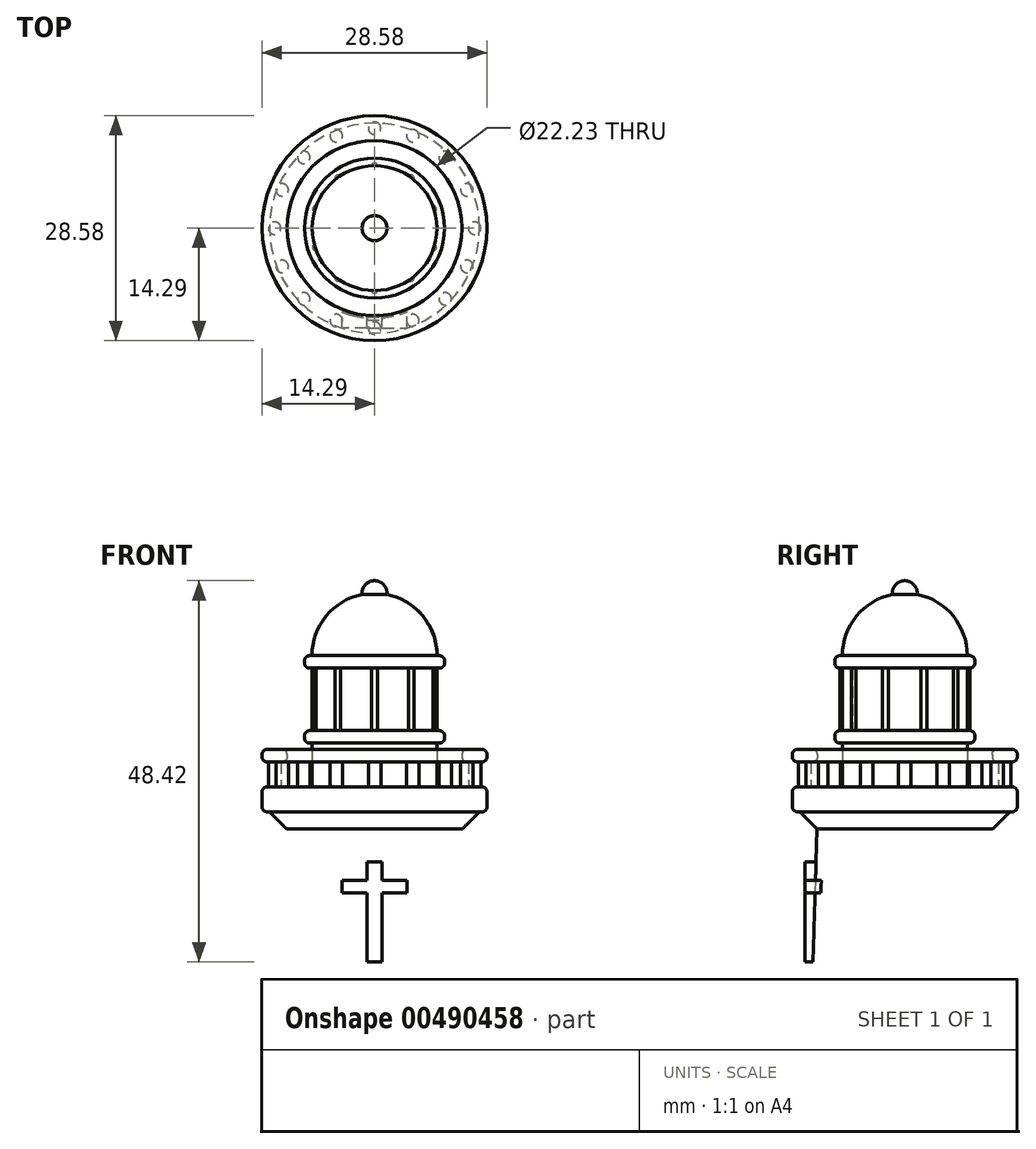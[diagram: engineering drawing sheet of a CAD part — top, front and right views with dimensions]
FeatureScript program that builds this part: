
annotation { "Feature Type Name" : "Feature", "Feature Type Description" : "" }
export const myFeature = defineFeature(function(context is Context, id is Id, definition is map)
    precondition{}
    {
        {
            var Q0;
            Q0=qCreatedBy(makeId("Top.planeOp"),FACE);
            var sketch = newSketch(context, id + "F0", { "sketchPlane" : qUnion([Q0])});
            skCircle(sketch, "E0.cCircle", {"center": v(0, 0) * mm, "radius": 25.4 * mm, "construction": true});
            skLineSegment(sketch, "E0.0", {"start": v(25.4, 14.66) * mm, "end": v(25.4, -14.66) * mm});
            skLineSegment(sketch, "E0.1", {"start": v(25.4, -14.66) * mm, "end": v(0, -29.33) * mm});
            skLineSegment(sketch, "E0.2", {"start": v(0, -29.33) * mm, "end": v(-25.4, -14.66) * mm});
            skLineSegment(sketch, "E0.3", {"start": v(-25.4, -14.66) * mm, "end": v(-25.4, 14.66) * mm});
            skLineSegment(sketch, "E0.4", {"start": v(-25.4, 14.66) * mm, "end": v(0, 29.33) * mm});
            skLineSegment(sketch, "E0.5", {"start": v(0, 29.33) * mm, "end": v(25.4, 14.66) * mm});
            skPoint(sketch, "E0.0.midPoint", {"position": v(25.4, 0) * mm});
            skSolve(sketch);
        }
        {
            var Q0;
            Q0 = qSketchRegion(id + "F0", true);
            extrude(context, id + "F1", {"entities" : qUnion([Q0]), "depth" : 3.17 * mm});
        }
        {
            var Q0;
            Q0=makeQuery(id+"F1.opExtrude","CAP_FACE",FACE,{"disambiguationData":[OSD([sQuery(id+"F0.wireOp",EDGE,"E0.0"),sQuery(id+"F0.wireOp",EDGE,"E0.1"),sQuery(id+"F0.wireOp",EDGE,"E0.2"),sQuery(id+"F0.wireOp",EDGE,"E0.3"),sQuery(id+"F0.wireOp",EDGE,"E0.4"),sQuery(id+"F0.wireOp",EDGE,"E0.5")])],"isStart":false});
            var sketch = newSketch(context, id + "F2", { "sketchPlane" : qUnion([Q0])});
            skCircle(sketch, "E1.cCircle", {"center": v(0, 0) * mm, "radius": 22.23 * mm, "construction": true});
            skLineSegment(sketch, "E1.0", {"start": v(22.23, 12.83) * mm, "end": v(22.23, -12.83) * mm});
            skLineSegment(sketch, "E1.1", {"start": v(22.23, -12.83) * mm, "end": v(0, -25.66) * mm});
            skLineSegment(sketch, "E1.2", {"start": v(0, -25.66) * mm, "end": v(-22.23, -12.83) * mm});
            skLineSegment(sketch, "E1.3", {"start": v(-22.22, -12.83) * mm, "end": v(-22.23, 12.83) * mm});
            skLineSegment(sketch, "E1.4", {"start": v(-22.23, 12.83) * mm, "end": v(0, 25.66) * mm});
            skLineSegment(sketch, "E1.5", {"start": v(0, 25.66) * mm, "end": v(22.22, 12.83) * mm});
            skPoint(sketch, "E1.0.midPoint", {"position": v(22.23, 0) * mm});
            skSolve(sketch);
        }
        {
            var Q0;
            Q0 = qSketchRegion(id + "F2", true);
            extrude(context, id + "F3", {"entities" : qUnion([Q0]), "operationType" : NewBodyOperationType.ADD, "depth" : 3.17 * mm});
        }
        {
            var Q0;
            Q0=makeQuery(id+"F3.opExtrude","CAP_FACE",FACE,{"disambiguationData":[OSD([sQuery(id+"F2.wireOp",EDGE,"E1.0"),sQuery(id+"F2.wireOp",EDGE,"E1.1"),sQuery(id+"F2.wireOp",EDGE,"E1.2"),sQuery(id+"F2.wireOp",EDGE,"E1.3"),sQuery(id+"F2.wireOp",EDGE,"E1.4"),sQuery(id+"F2.wireOp",EDGE,"E1.5")])],"isStart":false});
            var sketch = newSketch(context, id + "F4", { "sketchPlane" : qUnion([Q0])});
            skCircle(sketch, "E2.cCircle", {"center": v(0, 0) * mm, "radius": 19.05 * mm, "construction": true});
            skLineSegment(sketch, "E2.0", {"start": v(19.05, 11) * mm, "end": v(19.05, -11) * mm});
            skLineSegment(sketch, "E2.1", {"start": v(19.05, -11) * mm, "end": v(0, -22) * mm});
            skLineSegment(sketch, "E2.2", {"start": v(0, -22) * mm, "end": v(-19.05, -11) * mm});
            skLineSegment(sketch, "E2.3", {"start": v(-19.05, -11) * mm, "end": v(-19.05, 11) * mm});
            skLineSegment(sketch, "E2.4", {"start": v(-19.05, 11) * mm, "end": v(0, 22) * mm});
            skLineSegment(sketch, "E2.5", {"start": v(0, 22) * mm, "end": v(19.05, 11) * mm});
            skPoint(sketch, "E2.0.midPoint", {"position": v(19.05, 0) * mm});
            skSolve(sketch);
        }
        {
            var Q0;
            Q0 = qSketchRegion(id + "F4", true);
            extrude(context, id + "F5", {"entities" : qUnion([Q0]), "operationType" : NewBodyOperationType.ADD, "depth" : 3.17 * mm});
        }
        {
            var Q0;
            Q0=makeQuery(id+"F5.opExtrude","CAP_FACE",FACE,{"disambiguationData":[OSD([sQuery(id+"F4.wireOp",EDGE,"E2.0"),sQuery(id+"F4.wireOp",EDGE,"E2.1"),sQuery(id+"F4.wireOp",EDGE,"E2.2"),sQuery(id+"F4.wireOp",EDGE,"E2.3"),sQuery(id+"F4.wireOp",EDGE,"E2.4"),sQuery(id+"F4.wireOp",EDGE,"E2.5")])],"isStart":false});
            var sketch = newSketch(context, id + "F6", { "sketchPlane" : qUnion([Q0])});
            skCircle(sketch, "E3", {"center": v(0, 0) * mm, "radius": 12.7 * mm});
            skSolve(sketch);
        }
        {
            var Q0;
            Q0 = qSketchRegion(id + "F6", true);
            extrude(context, id + "F7", {"entities" : qUnion([Q0]), "operationType" : NewBodyOperationType.ADD, "depth" : 50.8 * mm});
        }
        {
            var Q0;
            Q0=qCreatedBy(makeId("Right.planeOp"),FACE);
            var sketch = newSketch(context, id + "F8", { "sketchPlane" : qUnion([Q0])});
            skLineSegment(sketch, "E4", {"start": v(-11.11, 60.33) * mm, "end": v(-12.7, 9.52) * mm});
            skLineSegment(sketch, "E5", {"start": v(-12.7, 9.52) * mm, "end": v(-12.7, 60.33) * mm});
            skLineSegment(sketch, "E6", {"start": v(-12.7, 60.33) * mm, "end": v(-11.11, 60.33) * mm});
            skLineSegment(sketch, "E7", {"start": v(0, 59.88) * mm, "end": v(0, 51.38) * mm, "construction": true});
            skSolve(sketch);
        }
        {
            var Q0;
            Q0 = qSketchRegion(id + "F8", true);
            var Q1;
            Q1=sQuery(id+"F8.wireOp",EDGE,"E7");
            revolve(context, id + "F9", {"operationType" : NewBodyOperationType.REMOVE, "entities" : qUnion([Q0]), "axis" : qUnion([Q1]), "revolveType" : RevolveType.FULL, "oppositeDirection" : true});
        }
        {
            var Q0;
            Q0=qCreatedBy(makeId("Front.planeOp"),FACE);
            var sketch = newSketch(context, id + "F10", { "sketchPlane" : qUnion([Q0])});
            skLineSegment(sketch, "E8.bottom", {"start": v(0, 53.98) * mm, "end": v(0.95, 53.98) * mm});
            skLineSegment(sketch, "E8.top", {"start": v(0, 41.28) * mm, "end": v(0.95, 41.28) * mm});
            skLineSegment(sketch, "E8.left", {"start": v(0, 53.98) * mm, "end": v(0, 41.28) * mm});
            skLineSegment(sketch, "E8.right", {"start": v(0.95, 53.98) * mm, "end": v(0.95, 51.6) * mm});
            skLineSegment(sketch, "E9.bottom", {"start": v(0.95, 51.6) * mm, "end": v(4.13, 51.6) * mm});
            skLineSegment(sketch, "E9.top", {"start": v(0.95, 50) * mm, "end": v(4.13, 50) * mm});
            skLineSegment(sketch, "E9.right", {"start": v(4.13, 51.6) * mm, "end": v(4.13, 50) * mm});
            skLineSegment(sketch, "E10.trimOffspring", {"start": v(0.95, 50) * mm, "end": v(0.95, 41.28) * mm});
            skLineSegment(sketch, "E11.MirrorCS", {"start": v(0, 53.98) * mm, "end": v(-0.95, 53.98) * mm});
            skLineSegment(sketch, "E12.MirrorCS", {"start": v(-0.95, 53.98) * mm, "end": v(-0.95, 51.6) * mm});
            skLineSegment(sketch, "E13.MirrorCS", {"start": v(-0.95, 51.6) * mm, "end": v(-4.13, 51.6) * mm});
            skLineSegment(sketch, "E14.MirrorCS", {"start": v(-4.13, 51.6) * mm, "end": v(-4.13, 50) * mm});
            skLineSegment(sketch, "E15.MirrorCS", {"start": v(-0.95, 50) * mm, "end": v(-4.13, 50) * mm});
            skLineSegment(sketch, "E16.MirrorCS", {"start": v(-0.95, 50) * mm, "end": v(-0.95, 41.28) * mm});
            skLineSegment(sketch, "E17.MirrorCS", {"start": v(0, 41.28) * mm, "end": v(-0.95, 41.28) * mm});
            skSolve(sketch);
        }
        {
            var Q0;
            Q0 = qSketchRegion(id + "F10", true);
            extrude(context, id + "F11", {"entities" : qUnion([Q0]), "operationType" : NewBodyOperationType.ADD, "depth" : 12.7 * mm});
        }
        {
            var Q0;
            Q0=makeQuery(id+"F7.opExtrude","CAP_FACE",FACE,{"disambiguationData":[OSD([sQuery(id+"F6.wireOp",EDGE,"E3")])],"isStart":false});
            cPlane(context, id + "F12", {"entities" : qUnion([Q0]), "cplaneType" : CPlaneType.OFFSET, "offset" : 0 * mm, "oppositeDirection" : true, "width" : 152.4 * mm, "height" : 152.4 * mm});
        }
        {
            var Q0;
            Q0=qCreatedBy(id+"F12.planeOp",FACE);
            var sketch = newSketch(context, id + "F13", { "sketchPlane" : qUnion([Q0])});
            skCircle(sketch, "E18", {"center": v(0, 0) * mm, "radius": 14.29 * mm});
            skSolve(sketch);
        }
        {
            var Q0;
            Q0 = qSketchRegion(id + "F13", true);
            extrude(context, id + "F14", {"entities" : qUnion([Q0]), "operationType" : NewBodyOperationType.ADD, "depth" : 3.17 * mm});
        }
        {
            var Q0;
            Q0=makeQuery(id+"F14.opExtrude","CAP_FACE",FACE,{"disambiguationData":[OSD([sQuery(id+"F13.wireOp",EDGE,"E18")])],"isStart":false});
            var sketch = newSketch(context, id + "F15", { "sketchPlane" : qUnion([Q0])});
            skCircle(sketch, "E19", {"center": v(0, 0) * mm, "radius": 7.94 * mm});
            skSolve(sketch);
        }
        {
            var Q0;
            Q0 = qSketchRegion(id + "F15", true);
            extrude(context, id + "F16", {"entities" : qUnion([Q0]), "operationType" : NewBodyOperationType.ADD, "depth" : 15.88 * mm});
        }
        {
            var Q0;
            Q0=makeQuery(id+"F14.opExtrude","CAP_FACE",FACE,{"disambiguationData":[OSD([sQuery(id+"F13.wireOp",EDGE,"E18")])],"isStart":false});
            var sketch = newSketch(context, id + "F17", { "sketchPlane" : qUnion([Q0])});
            skCircle(sketch, "E20", {"center": v(0, 0) * mm, "radius": 12.7 * mm, "construction": true});
            skCircle(sketch, "E21", {"center": v(0, 12.7) * mm, "radius": 0.8 * mm});
            skCircle(sketch, "E22.1.1", {"center": v(-4.86, 11.73) * mm, "radius": 0.8 * mm});
            skCircle(sketch, "E22.2.1", {"center": v(-8.98, 8.98) * mm, "radius": 0.8 * mm});
            skCircle(sketch, "E23.2.3.0", {"center": v(-11.73, 4.86) * mm, "radius": 0.8 * mm});
            skCircle(sketch, "E23.2.4.0", {"center": v(-12.7, 0) * mm, "radius": 0.8 * mm});
            skCircle(sketch, "E23.2.5.0", {"center": v(-11.73, -4.86) * mm, "radius": 0.8 * mm});
            skCircle(sketch, "E23.2.6.0", {"center": v(-8.98, -8.98) * mm, "radius": 0.8 * mm});
            skCircle(sketch, "E23.2.7.0", {"center": v(-4.86, -11.73) * mm, "radius": 0.8 * mm});
            skCircle(sketch, "E23.2.8.0", {"center": v(0, -12.7) * mm, "radius": 0.8 * mm});
            skCircle(sketch, "E23.2.9.0", {"center": v(4.86, -11.73) * mm, "radius": 0.8 * mm});
            skCircle(sketch, "E23.2.10.0", {"center": v(8.98, -8.98) * mm, "radius": 0.8 * mm});
            skCircle(sketch, "E23.2.11.0", {"center": v(11.73, -4.86) * mm, "radius": 0.8 * mm});
            skCircle(sketch, "E23.2.12.0", {"center": v(12.7, 0) * mm, "radius": 0.8 * mm});
            skCircle(sketch, "E23.2.13.0", {"center": v(11.73, 4.86) * mm, "radius": 0.8 * mm});
            skCircle(sketch, "E23.2.14.0", {"center": v(8.98, 8.98) * mm, "radius": 0.8 * mm});
            skCircle(sketch, "E24.2.15.0", {"center": v(4.86, 11.73) * mm, "radius": 0.8 * mm});
            skSolve(sketch);
        }
        {
            var Q0;
            Q0 = qSketchRegion(id + "F17", true);
            extrude(context, id + "F18", {"entities" : qUnion([Q0]), "operationType" : NewBodyOperationType.ADD, "depth" : 3.17 * mm});
        }
        {
            var Q0;
            Q0=makeQuery(id+"F18.opExtrude","CAP_FACE",FACE,{"disambiguationData":[OSD([sQuery(id+"F17.wireOp",EDGE,"E23.2.12.0")])],"isStart":false});
            cPlane(context, id + "F19", {"entities" : qUnion([Q0]), "cplaneType" : CPlaneType.OFFSET, "offset" : 0 * mm, "width" : 152.4 * mm, "height" : 152.4 * mm});
        }
        {
            var Q0;
            Q0=qCreatedBy(id+"F19.planeOp",FACE);
            var sketch = newSketch(context, id + "F20", { "sketchPlane" : qUnion([Q0])});
            skCircle(sketch, "E25", {"center": v(0, 0) * mm, "radius": 14.29 * mm});
            skCircle(sketch, "E26", {"center": v(0, 0) * mm, "radius": 11.11 * mm});
            skSolve(sketch);
        }
        {
            var Q0;
            Q0 = qSketchRegion(id + "F20", true);
            extrude(context, id + "F21", {"entities" : qUnion([Q0]), "operationType" : NewBodyOperationType.ADD, "depth" : 1.59 * mm});
        }
        {
            var Q0;
            Q0=qCreatedBy(makeId("Front.planeOp"),FACE);
            var sketch = newSketch(context, id + "F22", { "sketchPlane" : qUnion([Q0])});
            skLineSegment(sketch, "E27", {"start": v(10.8, 57.79) * mm, "end": v(13.33, 60.33) * mm});
            skLineSegment(sketch, "E28", {"start": v(13.33, 60.33) * mm, "end": v(10.8, 60.33) * mm});
            skLineSegment(sketch, "E29", {"start": v(10.8, 60.33) * mm, "end": v(10.8, 57.79) * mm});
            skLineSegment(sketch, "E30", {"start": v(0, 59.54) * mm, "end": v(0, 56.04) * mm, "construction": true});
            skSolve(sketch);
        }
        {
            var Q0;
            Q0 = qSketchRegion(id + "F22", true);
            var Q1;
            Q1=sQuery(id+"F22.wireOp",EDGE,"E30");
            revolve(context, id + "F23", {"operationType" : NewBodyOperationType.ADD, "entities" : qUnion([Q0]), "axis" : qUnion([Q1]), "revolveType" : RevolveType.FULL});
        }
        {
            var Q0;
            Q0=makeQuery(id+"F21.opExtrude","CAP_FACE",FACE,{"disambiguationData":[OSD([sQuery(id+"F20.wireOp",EDGE,"E25"),sQuery(id+"F20.wireOp",EDGE,"E26")])],"isStart":false});
            cPlane(context, id + "F24", {"entities" : qUnion([Q0]), "cplaneType" : CPlaneType.OFFSET, "offset" : 1.59 * mm, "width" : 152.4 * mm, "height" : 152.4 * mm});
        }
        {
            var Q0;
            Q0=qCreatedBy(id+"F24.planeOp",FACE);
            var sketch = newSketch(context, id + "F25", { "sketchPlane" : qUnion([Q0])});
            skCircle(sketch, "E31", {"center": v(0, 0) * mm, "radius": 8.9 * mm});
            skCircle(sketch, "E32", {"center": v(0, 0) * mm, "radius": 6.35 * mm});
            skSolve(sketch);
        }
        {
            var Q0;
            Q0 = qSketchRegion(id + "F25", true);
            extrude(context, id + "F26", {"entities" : qUnion([Q0]), "operationType" : NewBodyOperationType.ADD, "endBound" : BoundingType.SYMMETRIC, "depth" : 1.59 * mm});
        }
        {
            var Q0;
            Q0=makeQuery(id+"F16.opExtrude","CAP_FACE",FACE,{"disambiguationData":[OSD([sQuery(id+"F15.wireOp",EDGE,"E19")])],"isStart":false});
            var sketch = newSketch(context, id + "F27", { "sketchPlane" : qUnion([Q0])});
            skCircle(sketch, "E33", {"center": v(0, 0) * mm, "radius": 8.9 * mm});
            skSolve(sketch);
        }
        {
            var Q0;
            Q0 = qSketchRegion(id + "F27", true);
            extrude(context, id + "F28", {"entities" : qUnion([Q0]), "operationType" : NewBodyOperationType.ADD, "endBound" : BoundingType.SYMMETRIC, "depth" : 1.59 * mm});
        }
        {
            var Q0;
            Q0=qCreatedBy(makeId("Front.planeOp"),FACE);
            var sketch = newSketch(context, id + "F29", { "sketchPlane" : qUnion([Q0])});
            skArc(sketch, "E34", {"start": v(7.94, 80.17) * mm, "mid": v(5.61, 85.78) * mm, "end": v(0, 88.1) * mm});
            skLineSegment(sketch, "E35", {"start": v(0, 88.1) * mm, "end": v(0, 80.17) * mm});
            skLineSegment(sketch, "E36", {"start": v(0, 80.17) * mm, "end": v(7.94, 80.17) * mm});
            skSolve(sketch);
        }
        {
            var Q0;
            Q0 = qSketchRegion(id + "F29", true);
            var Q1;
            Q1=sQuery(id+"F29.wireOp",EDGE,"E35");
            revolve(context, id + "F30", {"operationType" : NewBodyOperationType.ADD, "entities" : qUnion([Q0]), "axis" : qUnion([Q1]), "revolveType" : RevolveType.FULL});
        }
        {
            var Q0;
            Q0=makeQuery(id+"F14.opExtrude","CAP_EDGE",EDGE,{"disambiguationData":[OSD([sQuery(id+"F13.wireOp",EDGE,"E18")])],"isStart":true});
            var Q1;
            Q1=makeQuery(id+"F14.opExtrude","CAP_EDGE",EDGE,{"disambiguationData":[OSD([sQuery(id+"F13.wireOp",EDGE,"E18")])],"isStart":false});
            var Q2;
            Q2=makeQuery(id+"F26.opExtrude","CAP_EDGE",EDGE,{"disambiguationData":[OSD([sQuery(id+"F25.wireOp",EDGE,"E31")])],"isStart":true});
            var Q3;
            Q3=makeQuery(id+"F26.opExtrude","CAP_EDGE",EDGE,{"disambiguationData":[OSD([sQuery(id+"F25.wireOp",EDGE,"E31")])],"isStart":false});
            var Q4;
            Q4=makeQuery(id+"F28.opExtrude","CAP_EDGE",EDGE,{"disambiguationData":[OSD([sQuery(id+"F27.wireOp",EDGE,"E33")])],"isStart":true});
            var Q5;
            Q5=makeQuery(id+"F28.opExtrude","CAP_EDGE",EDGE,{"disambiguationData":[OSD([sQuery(id+"F27.wireOp",EDGE,"E33")])],"isStart":false});
            var Q6;
            Q6=makeQuery(id+"F21.opExtrude","CAP_EDGE",EDGE,{"disambiguationData":[OSD([sQuery(id+"F20.wireOp",EDGE,"E25")])],"isStart":true});
            var Q7;
            Q7=makeQuery(id+"F21.opExtrude","CAP_EDGE",EDGE,{"disambiguationData":[OSD([sQuery(id+"F20.wireOp",EDGE,"E25")])],"isStart":false});
            var Q8;
            Q8=makeQuery(id+"F21.opExtrude","CAP_EDGE",EDGE,{"disambiguationData":[OSD([sQuery(id+"F20.wireOp",EDGE,"E26")])],"isStart":false});
            var Q9;
            Q9=makeQuery(id+"F21.opExtrude","CAP_EDGE",EDGE,{"disambiguationData":[OSD([sQuery(id+"F20.wireOp",EDGE,"E26")])],"isStart":true});
            fillet(context, id + "F31", {"entities" : qUnion([Q0, Q1, Q2, Q3, Q4, Q5, Q6, Q7, Q8, Q9]), "radius" : 0.64 * mm, "tangentPropagation" : true, "allowEdgeOverflow" : false});
        }
        {
            var Q0;
            Q0=qCreatedBy(makeId("Front.planeOp"),FACE);
            var sketch = newSketch(context, id + "F32", { "sketchPlane" : qUnion([Q0])});
            skArc(sketch, "E37", {"start": v(0, 86.52) * mm, "mid": v(1.59, 88.1) * mm, "end": v(0, 89.7) * mm});
            skLineSegment(sketch, "E38", {"start": v(0, 89.7) * mm, "end": v(0, 86.52) * mm});
            skSolve(sketch);
        }
        {
            var Q0;
            Q0 = qSketchRegion(id + "F32", true);
            var Q1;
            Q1=sQuery(id+"F32.wireOp",EDGE,"E38");
            revolve(context, id + "F33", {"operationType" : NewBodyOperationType.ADD, "entities" : qUnion([Q0]), "axis" : qUnion([Q1]), "revolveType" : RevolveType.FULL});
        }
        {
            var Q0;
            Q0=qCreatedBy(makeId("Front.planeOp"),FACE);
            var sketch = newSketch(context, id + "F34", { "sketchPlane" : qUnion([Q0])});
            skLineSegment(sketch, "E39.bottom", {"start": v(0, 9.53) * mm, "end": v(3.18, 9.53) * mm});
            skLineSegment(sketch, "E39.top", {"start": v(0, 15.88) * mm, "end": v(3.17, 15.88) * mm});
            skLineSegment(sketch, "E39.left", {"start": v(0, 9.53) * mm, "end": v(0, 15.88) * mm});
            skLineSegment(sketch, "E39.right", {"start": v(3.17, 9.53) * mm, "end": v(3.17, 15.88) * mm});
            skArc(sketch, "E40", {"start": v(3.17, 15.88) * mm, "mid": v(2.25, 18.12) * mm, "end": v(0, 19.05) * mm});
            skArc(sketch, "E41.MirrorCS", {"start": v(-3.17, 15.88) * mm, "mid": v(-2.25, 18.12) * mm, "end": v(0, 19.05) * mm});
            skLineSegment(sketch, "E42.MirrorCS", {"start": v(-3.17, 9.53) * mm, "end": v(-3.18, 15.88) * mm});
            skLineSegment(sketch, "E43.MirrorCS", {"start": v(0, 9.53) * mm, "end": v(-3.17, 9.53) * mm});
            skSolve(sketch);
        }
        {
            var Q0;
            Q0 = qSketchRegion(id + "F34", true);
            extrude(context, id + "F35", {"entities" : qUnion([Q0]), "operationType" : NewBodyOperationType.ADD, "depth" : 15.24 * mm});
        }
        {
            var Q0;
            Q0=makeQuery(id+"F1.opExtrude","CAP_FACE",FACE,{"disambiguationData":[OSD([sQuery(id+"F0.wireOp",EDGE,"E0.0"),sQuery(id+"F0.wireOp",EDGE,"E0.1"),sQuery(id+"F0.wireOp",EDGE,"E0.2"),sQuery(id+"F0.wireOp",EDGE,"E0.3"),sQuery(id+"F0.wireOp",EDGE,"E0.4"),sQuery(id+"F0.wireOp",EDGE,"E0.5")])],"isStart":true});
            var sketch = newSketch(context, id + "F36", { "sketchPlane" : qUnion([Q0])});
            skCircle(sketch, "E44", {"center": v(0, 0) * mm, "radius": 5.72 * mm});
            skSolve(sketch);
        }
        {
            var Q0;
            Q0 = qSketchRegion(id + "F36", true);
            extrude(context, id + "F37", {"entities" : qUnion([Q0]), "operationType" : NewBodyOperationType.REMOVE, "oppositeDirection" : true, "depth" : 79.38 * mm});
        }
        {
            var Q0;
            Q0=makeQuery(id+"F1.opExtrude","CAP_FACE",FACE,{"disambiguationData":[OSD([sQuery(id+"F0.wireOp",EDGE,"E0.0"),sQuery(id+"F0.wireOp",EDGE,"E0.1"),sQuery(id+"F0.wireOp",EDGE,"E0.2"),sQuery(id+"F0.wireOp",EDGE,"E0.3"),sQuery(id+"F0.wireOp",EDGE,"E0.4"),sQuery(id+"F0.wireOp",EDGE,"E0.5")])],"isStart":true});
            var sketch = newSketch(context, id + "F38", { "sketchPlane" : qUnion([Q0])});
            skCircle(sketch, "E45", {"center": v(0, 0) * mm, "radius": 7.94 * mm});
            skSolve(sketch);
        }
        {
            var Q0;
            Q0 = qSketchRegion(id + "F38", true);
            extrude(context, id + "F39", {"entities" : qUnion([Q0]), "operationType" : NewBodyOperationType.REMOVE, "oppositeDirection" : true, "depth" : 57.15 * mm});
        }
        {
            var Q0;
            Q0=makeQuery(id+"F3.opExtrude","SWEPT_FACE",FACE,{"disambiguationData":[OSD([sQuery(id+"F2.wireOp",EDGE,"E1.2")])]});
            var sketch = newSketch(context, id + "F40", { "sketchPlane" : qUnion([Q0])});
            skText(sketch, "E46", { "text": "MIZPAH", "fontName": "OpenSans-Bold.ttf"});
            skLineSegment(sketch, "E47", {"start": v(-12.83, 6.35) * mm, "end": v(0, 6.35) * mm, "construction": true});
            skLineSegment(sketch, "E48", {"start": v(0, 6.35) * mm, "end": v(12.83, 6.35) * mm, "construction": true});
            const initialGuessF40  = {"E46": [-0.00862, 0.00318, 1, 0, 0.00317]};
            skSetInitialGuess(sketch, initialGuessF40);
            skSolve(sketch);
        }
        {
            var Q0;
            Q0 = qSketchRegion(id + "F40", true);
            extrude(context, id + "F41", {"entities" : qUnion([Q0]), "operationType" : NewBodyOperationType.ADD, "depth" : 1.59 * mm});
        }
        {
            var Q0;
            Q0=makeQuery(id+"F3.opExtrude","SWEPT_FACE",FACE,{"disambiguationData":[OSD([sQuery(id+"F2.wireOp",EDGE,"E1.1")])]});
            var sketch = newSketch(context, id + "F42", { "sketchPlane" : qUnion([Q0])});
            skText(sketch, "E49", { "text": "GEN. 31:49", "fontName": "OpenSans-Bold.ttf"});
            skLineSegment(sketch, "E50", {"start": v(0, 6.35) * mm, "end": v(-12.83, 6.35) * mm, "construction": true});
            skLineSegment(sketch, "E51", {"start": v(0, 6.35) * mm, "end": v(12.83, 6.35) * mm, "construction": true});
            const initialGuessF42  = {"E49": [-0.01155, 0.00318, 1, 0, 0.00317]};
            skSetInitialGuess(sketch, initialGuessF42);
            skSolve(sketch);
        }
        {
            var Q0;
            Q0 = qSketchRegion(id + "F42", true);
            extrude(context, id + "F43", {"entities" : qUnion([Q0]), "operationType" : NewBodyOperationType.ADD, "depth" : 1.59 * mm});
        }
        {
            var Q0;
            Q0=makeQuery(id+"F26.opExtrude","CAP_FACE",FACE,{"disambiguationData":[OSD([sQuery(id+"F25.wireOp",EDGE,"E31"),sQuery(id+"F25.wireOp",EDGE,"E32")])],"isStart":false});
            cPlane(context, id + "F44", {"entities" : qUnion([Q0]), "cplaneType" : CPlaneType.OFFSET, "offset" : 0 * mm, "width" : 152.4 * mm, "height" : 152.4 * mm});
        }
        {
            var Q0;
            Q0=qCreatedBy(id+"F44.planeOp",FACE);
            var sketch = newSketch(context, id + "F45", { "sketchPlane" : qUnion([Q0])});
            skCircle(sketch, "E52", {"center": v(0, 0) * mm, "radius": 8.26 * mm, "construction": true});
            skCircle(sketch, "E53", {"center": v(0, 7.84) * mm, "radius": 0.41 * mm});
            skCircle(sketch, "E54.1.0", {"center": v(-4.6, 6.34) * mm, "radius": 0.41 * mm});
            skCircle(sketch, "E54.2.0", {"center": v(-7.46, 2.42) * mm, "radius": 0.41 * mm});
            skCircle(sketch, "E54.3.0", {"center": v(-7.46, -2.42) * mm, "radius": 0.41 * mm});
            skCircle(sketch, "E54.4.0", {"center": v(-4.6, -6.34) * mm, "radius": 0.41 * mm});
            skCircle(sketch, "E54.5.0", {"center": v(0, -7.84) * mm, "radius": 0.41 * mm});
            skCircle(sketch, "E54.6.0", {"center": v(4.6, -6.34) * mm, "radius": 0.41 * mm});
            skCircle(sketch, "E54.7.0", {"center": v(7.46, -2.42) * mm, "radius": 0.41 * mm});
            skCircle(sketch, "E54.8.0", {"center": v(7.46, 2.42) * mm, "radius": 0.41 * mm});
            skCircle(sketch, "E54.9.0", {"center": v(4.6, 6.34) * mm, "radius": 0.41 * mm});
            skSolve(sketch);
        }
        {
            var Q0;
            Q0 = qSketchRegion(id + "F45", true);
            extrude(context, id + "F46", {"entities" : qUnion([Q0]), "operationType" : NewBodyOperationType.ADD, "depth" : 8.9 * mm});
        }
        {
            var Q0;
            Q0=qCreatedBy(id+"F44.planeOp",FACE);
            var sketch = newSketch(context, id + "F47", { "sketchPlane" : qUnion([Q0])});
            skCircle(sketch, "E55", {"center": v(0, 0) * mm, "radius": 6.99 * mm});
            skSolve(sketch);
        }
        {
            var Q0;
            Q0 = qSketchRegion(id + "F47", true);
            extrude(context, id + "F48", {"entities" : qUnion([Q0]), "operationType" : NewBodyOperationType.REMOVE, "depth" : 7.94 * mm});
        }
    });
